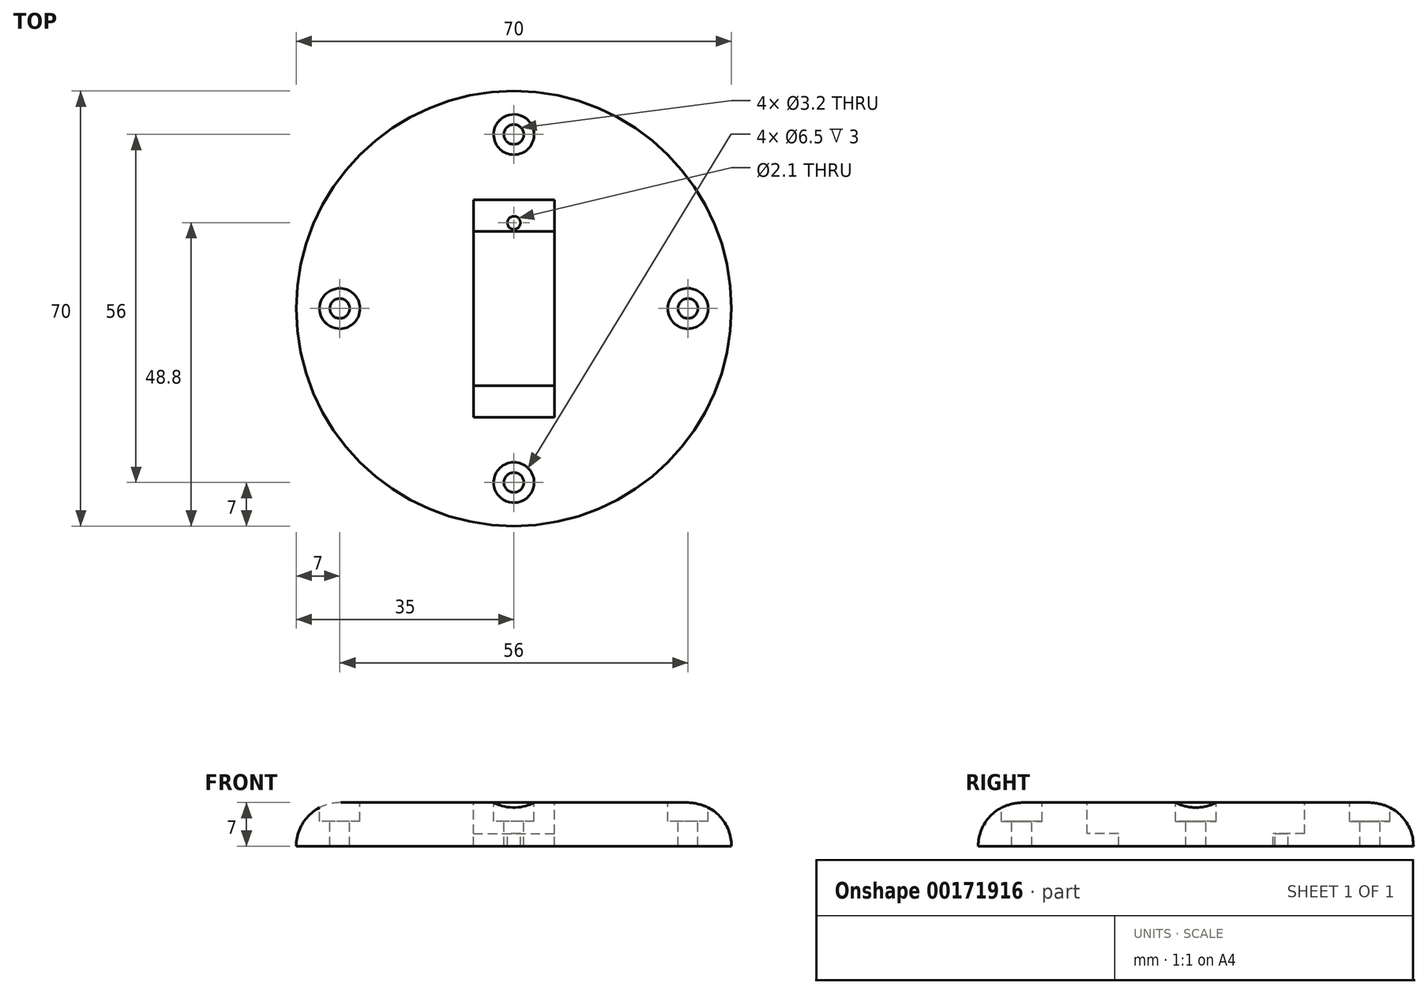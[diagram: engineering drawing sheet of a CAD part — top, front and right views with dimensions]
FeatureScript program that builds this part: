
annotation { "Feature Type Name" : "Feature", "Feature Type Description" : "" }
export const myFeature = defineFeature(function(context is Context, id is Id, definition is map)
    precondition{}
    {
        {
            var Q0;
            Q0=qCreatedBy(makeId("Top.planeOp"),FACE);
            var sketch = newSketch(context, id + "F0", { "sketchPlane" : qUnion([Q0])});
            skLineSegment(sketch, "E0.bottom", {"start": v(35, -35) * mm, "end": v(-35, -35) * mm});
            skLineSegment(sketch, "E0.top", {"start": v(35, 35) * mm, "end": v(-35, 35) * mm});
            skLineSegment(sketch, "E0.left", {"start": v(35, -35) * mm, "end": v(35, 35) * mm});
            skLineSegment(sketch, "E0.right", {"start": v(-35, -35) * mm, "end": v(-35, 35) * mm});
            skPoint(sketch, "E0.middle", {"position": v(0, 0) * mm});
            skSolve(sketch);
        }
        {
            var Q0;
            Q0 = qSketchRegion(id + "F0", true);
            extrude(context, id + "F1", {"entities" : qUnion([Q0]), "depth" : 10 * mm});
        }
        {
            var Q0;
            Q0=makeQuery(id+"F1.opExtrude","CAP_FACE",FACE,{"disambiguationData":[OSD([sQuery(id+"F0.wireOp",EDGE,"E0.bottom"),sQuery(id+"F0.wireOp",EDGE,"E0.top"),sQuery(id+"F0.wireOp",EDGE,"E0.left"),sQuery(id+"F0.wireOp",EDGE,"E0.right")])],"isStart":false});
            var sketch = newSketch(context, id + "F2", { "sketchPlane" : qUnion([Q0])});
            skLineSegment(sketch, "E1.bottom", {"start": v(6.5, -12.4) * mm, "end": v(-6.5, -12.4) * mm});
            skLineSegment(sketch, "E1.top", {"start": v(6.5, 12.4) * mm, "end": v(-6.5, 12.4) * mm});
            skLineSegment(sketch, "E1.left", {"start": v(6.5, -12.4) * mm, "end": v(6.5, 12.4) * mm});
            skLineSegment(sketch, "E1.right", {"start": v(-6.5, -12.4) * mm, "end": v(-6.5, 12.4) * mm});
            skPoint(sketch, "E1.middle", {"position": v(0, 0) * mm});
            skSolve(sketch);
        }
        {
            var Q0;
            Q0 = qSketchRegion(id + "F2", true);
            extrude(context, id + "F3", {"entities" : qUnion([Q0]), "operationType" : NewBodyOperationType.REMOVE, "oppositeDirection" : true, "depth" : 25 * mm});
        }
        {
            var Q0;
            Q0=makeQuery(id+"F1.opExtrude","CAP_FACE",FACE,{"disambiguationData":[OSD([sQuery(id+"F0.wireOp",EDGE,"E0.bottom"),sQuery(id+"F0.wireOp",EDGE,"E0.top"),sQuery(id+"F0.wireOp",EDGE,"E0.left"),sQuery(id+"F0.wireOp",EDGE,"E0.right")])],"isStart":false});
            var sketch = newSketch(context, id + "F4", { "sketchPlane" : qUnion([Q0])});
            skLineSegment(sketch, "E2.bottom", {"start": v(-20, 20) * mm, "end": v(20, 20) * mm});
            skLineSegment(sketch, "E2.top", {"start": v(-20, -20) * mm, "end": v(20, -20) * mm});
            skLineSegment(sketch, "E2.left", {"start": v(-20, 20) * mm, "end": v(-20, -20) * mm});
            skLineSegment(sketch, "E2.right", {"start": v(20, 20) * mm, "end": v(20, -20) * mm});
            skPoint(sketch, "E2.middle", {"position": v(0, 0) * mm});
            skSolve(sketch);
        }
        {
            var Q0;
            Q0=makeQuery(id+"F4.imprint","IMPRINT",FACE,{"disambiguationData":[TD([[makeQuery(id+"F4.imprint","IMPRINT",EDGE,{"derivedFrom":sQuery(id+"F4.wireOp",EDGE,"E2.bottom")}),1.0]])]});
            extrude(context, id + "F5", {"entities" : qUnion([Q0]), "operationType" : NewBodyOperationType.REMOVE, "oppositeDirection" : true, "depth" : 4 * mm});
        }
        {
            var Q0;
            Q0=makeQuery(id+"F1.opExtrude","CAP_FACE",FACE,{"disambiguationData":[OSD([sQuery(id+"F0.wireOp",EDGE,"E0.bottom"),sQuery(id+"F0.wireOp",EDGE,"E0.top"),sQuery(id+"F0.wireOp",EDGE,"E0.left"),sQuery(id+"F0.wireOp",EDGE,"E0.right")])],"isStart":false});
            var sketch = newSketch(context, id + "F6", { "sketchPlane" : qUnion([Q0])});
            skLineSegment(sketch, "E3.bottom", {"start": v(-6.5, 17.5) * mm, "end": v(6.5, 17.5) * mm});
            skLineSegment(sketch, "E3.top", {"start": v(-6.5, -17.5) * mm, "end": v(6.5, -17.5) * mm});
            skLineSegment(sketch, "E3.left", {"start": v(-6.5, 17.5) * mm, "end": v(-6.5, -17.5) * mm});
            skLineSegment(sketch, "E3.right", {"start": v(6.5, 17.5) * mm, "end": v(6.5, -17.5) * mm});
            skPoint(sketch, "E3.middle", {"position": v(0, 0) * mm});
            skSolve(sketch);
        }
        {
            var Q0;
            Q0 = qSketchRegion(id + "F6", true);
            extrude(context, id + "F7", {"entities" : qUnion([Q0]), "operationType" : NewBodyOperationType.REMOVE, "oppositeDirection" : true, "depth" : 9 * mm});
        }
        {
            var Q0;
            {var subQ0=sQuery(id+"F6.wireOp",EDGE,"E3.bottom");var subQ1=sQuery(id+"F6.wireOp",EDGE,"E3.left");var subQ2=sQuery(id+"F6.wireOp",EDGE,"E3.right");Q0=makeQuery(id+"F7.boolean.opBoolean","COPY",FACE,{"disambiguationData":[TD([makeQuery(id+"F3.boolean.opBoolean","COPY",FACE,{"derivedFrom":makeQuery(id+"F3.opExtrude","SWEPT_FACE",FACE,{"disambiguationData":[OSD([sQuery(id+"F2.wireOp",EDGE,"E1.top")])]})})])],"derivedFrom":makeQuery(id+"F7.opExtrude","CAP_FACE",FACE,{"disambiguationData":[OSD([subQ0,sQuery(id+"F6.wireOp",EDGE,"E3.top"),subQ1,subQ2])],"isStart":false})});}
            var sketch = newSketch(context, id + "F8", { "sketchPlane" : qUnion([Q0])});
            skCircle(sketch, "E4", {"center": v(0, 13.8) * mm, "radius": 1.05 * mm});
            skPoint(sketch, "E4.centerSnap0", {"position": v(0, 12.4) * mm});
            skCircle(sketch, "E5.MirrorC", {"center": v(0, -13.8) * mm, "radius": 1.05 * mm});
            skSolve(sketch);
        }
        {
            var Q0;
            Q0=makeQuery(id+"F8.imprint","IMPRINT",FACE,{"disambiguationData":[TD([[makeQuery(id+"F8.imprint","IMPRINT",EDGE,{"derivedFrom":sQuery(id+"F8.wireOp",EDGE,"E4")}),1.0]])]});
            var Q1;
            Q1=makeQuery(id+"F8.imprint","IMPRINT",FACE,{"disambiguationData":[TD([[makeQuery(id+"F8.imprint","IMPRINT",EDGE,{"derivedFrom":sQuery(id+"F8.wireOp",EDGE,"E5.MirrorC")}),-1.0]])]});
            extrude(context, id + "F9", {"entities" : qUnion([Q0, Q1]), "operationType" : NewBodyOperationType.REMOVE, "oppositeDirection" : true, "depth" : 25 * mm});
        }
        {
            var Q0;
            Q0=makeQuery(id+"F5.boolean.opBoolean","COPY",FACE,{"derivedFrom":makeQuery(id+"F5.opExtrude","CAP_FACE",FACE,{"disambiguationData":[OSD([sQuery(id+"F0.wireOp",EDGE,"E0.bottom"),sQuery(id+"F0.wireOp",EDGE,"E0.top"),sQuery(id+"F0.wireOp",EDGE,"E0.left"),sQuery(id+"F0.wireOp",EDGE,"E0.right"),sQuery(id+"F4.wireOp",EDGE,"E2.bottom"),sQuery(id+"F4.wireOp",EDGE,"E2.top"),sQuery(id+"F4.wireOp",EDGE,"E2.left"),sQuery(id+"F4.wireOp",EDGE,"E2.right")])],"isStart":false})});
            var sketch = newSketch(context, id + "F10", { "sketchPlane" : qUnion([Q0])});
            skCircle(sketch, "E6", {"center": v(-28, 0) * mm, "radius": 1.6 * mm});
            skCircle(sketch, "E7.MirrorC", {"center": v(28, 0) * mm, "radius": 1.6 * mm});
            skCircle(sketch, "E8", {"center": v(0, -28) * mm, "radius": 1.6 * mm});
            skCircle(sketch, "E9.MirrorC", {"center": v(0, 28) * mm, "radius": 1.6 * mm});
            skSolve(sketch);
        }
        {
            var Q0;
            Q0 = qSketchRegion(id + "F10", true);
            extrude(context, id + "F11", {"entities" : qUnion([Q0]), "operationType" : NewBodyOperationType.REMOVE, "oppositeDirection" : true, "depth" : 25 * mm});
        }
        {
            var Q0;
            Q0=makeQuery(id+"F5.boolean.opBoolean","COPY",FACE,{"derivedFrom":makeQuery(id+"F5.opExtrude","CAP_FACE",FACE,{"disambiguationData":[OSD([sQuery(id+"F0.wireOp",EDGE,"E0.bottom"),sQuery(id+"F0.wireOp",EDGE,"E0.top"),sQuery(id+"F0.wireOp",EDGE,"E0.left"),sQuery(id+"F0.wireOp",EDGE,"E0.right"),sQuery(id+"F4.wireOp",EDGE,"E2.bottom"),sQuery(id+"F4.wireOp",EDGE,"E2.top"),sQuery(id+"F4.wireOp",EDGE,"E2.left"),sQuery(id+"F4.wireOp",EDGE,"E2.right")])],"isStart":false})});
            var sketch = newSketch(context, id + "F12", { "sketchPlane" : qUnion([Q0])});
            skCircle(sketch, "E10", {"center": v(-28, 0) * mm, "radius": 3.25 * mm});
            skCircle(sketch, "E11.MirrorC", {"center": v(28, 0) * mm, "radius": 3.25 * mm});
            skCircle(sketch, "E12", {"center": v(0, -28) * mm, "radius": 3.25 * mm});
            skCircle(sketch, "E13.MirrorC", {"center": v(0, 28) * mm, "radius": 3.25 * mm});
            skSolve(sketch);
        }
        {
            var Q0;
            Q0 = qSketchRegion(id + "F12", true);
            extrude(context, id + "F13", {"entities" : qUnion([Q0]), "operationType" : NewBodyOperationType.REMOVE, "oppositeDirection" : true, "depth" : 3 * mm});
        }
        {
            var Q0;
            Q0=makeQuery(id+"F1.opExtrude","CAP_FACE",FACE,{"disambiguationData":[OSD([sQuery(id+"F0.wireOp",EDGE,"E0.bottom"),sQuery(id+"F0.wireOp",EDGE,"E0.top"),sQuery(id+"F0.wireOp",EDGE,"E0.left"),sQuery(id+"F0.wireOp",EDGE,"E0.right")])],"isStart":false});
            var Q1;
            Q1=makeQuery(id+"F5.boolean.opBoolean","COPY",FACE,{"derivedFrom":makeQuery(id+"F5.opExtrude","CAP_FACE",FACE,{"disambiguationData":[OSD([sQuery(id+"F0.wireOp",EDGE,"E0.bottom"),sQuery(id+"F0.wireOp",EDGE,"E0.top"),sQuery(id+"F0.wireOp",EDGE,"E0.left"),sQuery(id+"F0.wireOp",EDGE,"E0.right"),sQuery(id+"F4.wireOp",EDGE,"E2.bottom"),sQuery(id+"F4.wireOp",EDGE,"E2.top"),sQuery(id+"F4.wireOp",EDGE,"E2.left"),sQuery(id+"F4.wireOp",EDGE,"E2.right")])],"isStart":false})});
            extrude(context, id + "F14", {"entities" : qUnion([Q0]), "operationType" : NewBodyOperationType.REMOVE, "endBound" : BoundingType.UP_TO_SURFACE, "oppositeDirection" : true, "endBoundEntityFace" : qUnion([Q1]), "depth" : 25 * mm});
        }
        {
            var Q0;
            Q0=makeQuery(id+"F1.opExtrude","SWEPT_EDGE",EDGE,{"disambiguationData":[OSD([sQuery(id+"F0.wireOp",EDGE,"E0.bottom"),sQuery(id+"F0.wireOp",EDGE,"E0.right")])]});
            var Q1;
            Q1=makeQuery(id+"F1.opExtrude","SWEPT_EDGE",EDGE,{"disambiguationData":[OSD([sQuery(id+"F0.wireOp",EDGE,"E0.bottom"),sQuery(id+"F0.wireOp",EDGE,"E0.left")])]});
            var Q2;
            Q2=makeQuery(id+"F1.opExtrude","SWEPT_EDGE",EDGE,{"disambiguationData":[OSD([sQuery(id+"F0.wireOp",EDGE,"E0.top"),sQuery(id+"F0.wireOp",EDGE,"E0.left")])]});
            var Q3;
            Q3=makeQuery(id+"F1.opExtrude","SWEPT_EDGE",EDGE,{"disambiguationData":[OSD([sQuery(id+"F0.wireOp",EDGE,"E0.top"),sQuery(id+"F0.wireOp",EDGE,"E0.right")])]});
            fillet(context, id + "F15", {"entities" : qUnion([Q0, Q1, Q2, Q3]), "radius" : 35 * mm, "tangentPropagation" : true, "allowEdgeOverflow" : false});
        }
        {
            var Q0;
            Q0=makeQuery(id+"F1.opExtrude","CAP_FACE",FACE,{"disambiguationData":[OSD([sQuery(id+"F0.wireOp",EDGE,"E0.bottom"),sQuery(id+"F0.wireOp",EDGE,"E0.top"),sQuery(id+"F0.wireOp",EDGE,"E0.left"),sQuery(id+"F0.wireOp",EDGE,"E0.right")])],"isStart":true});
            extrude(context, id + "F16", {"entities" : qUnion([Q0]), "operationType" : NewBodyOperationType.ADD, "depth" : 1 * mm});
        }
        {
            var Q0;
            {var subQ0=sQuery(id+"F4.wireOp",EDGE,"E2.right");var subQ1=sQuery(id+"F4.wireOp",EDGE,"E2.left");var subQ2=sQuery(id+"F4.wireOp",EDGE,"E2.top");var subQ3=sQuery(id+"F4.wireOp",EDGE,"E2.bottom");var subQ4=sQuery(id+"F0.wireOp",EDGE,"E0.right");var subQ5=sQuery(id+"F0.wireOp",EDGE,"E0.left");var subQ6=sQuery(id+"F0.wireOp",EDGE,"E0.top");var subQ7=sQuery(id+"F0.wireOp",EDGE,"E0.bottom");Q0=makeQuery(id+"F15.opFillet","BLEND_EDGE",EDGE,{"blendedFrom":[makeQuery(id+"F1.opExtrude","SWEPT_EDGE",EDGE,{"disambiguationData":[OSD([subQ7,subQ5])]}),makeQuery(id+"F14.boolean.opBoolean","MERGE",FACE,{"derivedFrom":[makeQuery(id+"F5.boolean.opBoolean","COPY",FACE,{"derivedFrom":makeQuery(id+"F5.opExtrude","CAP_FACE",FACE,{"disambiguationData":[OSD([subQ7,subQ6,subQ5,subQ4,subQ3,subQ2,subQ1,subQ0])],"isStart":false})}),makeQuery(id+"F14.opExtrude","CAP_FACE",FACE,{"disambiguationData":[OSD([subQ7,subQ6,subQ5,subQ4,subQ3,subQ2,subQ1,subQ0])],"isStart":false})]})],"blendedInto":[makeQuery(id+"F14.boolean.opBoolean","MERGE",FACE,{"derivedFrom":[makeQuery(id+"F5.boolean.opBoolean","COPY",FACE,{"derivedFrom":makeQuery(id+"F5.opExtrude","CAP_FACE",FACE,{"disambiguationData":[OSD([subQ7,subQ6,subQ5,subQ4,subQ3,subQ2,subQ1,subQ0])],"isStart":false})}),makeQuery(id+"F14.opExtrude","CAP_FACE",FACE,{"disambiguationData":[OSD([subQ7,subQ6,subQ5,subQ4,subQ3,subQ2,subQ1,subQ0])],"isStart":false})]})]});}
            fillet(context, id + "F17", {"entities" : qUnion([Q0]), "radius" : 7 * mm, "tangentPropagation" : true, "allowEdgeOverflow" : false});
        }
    });
